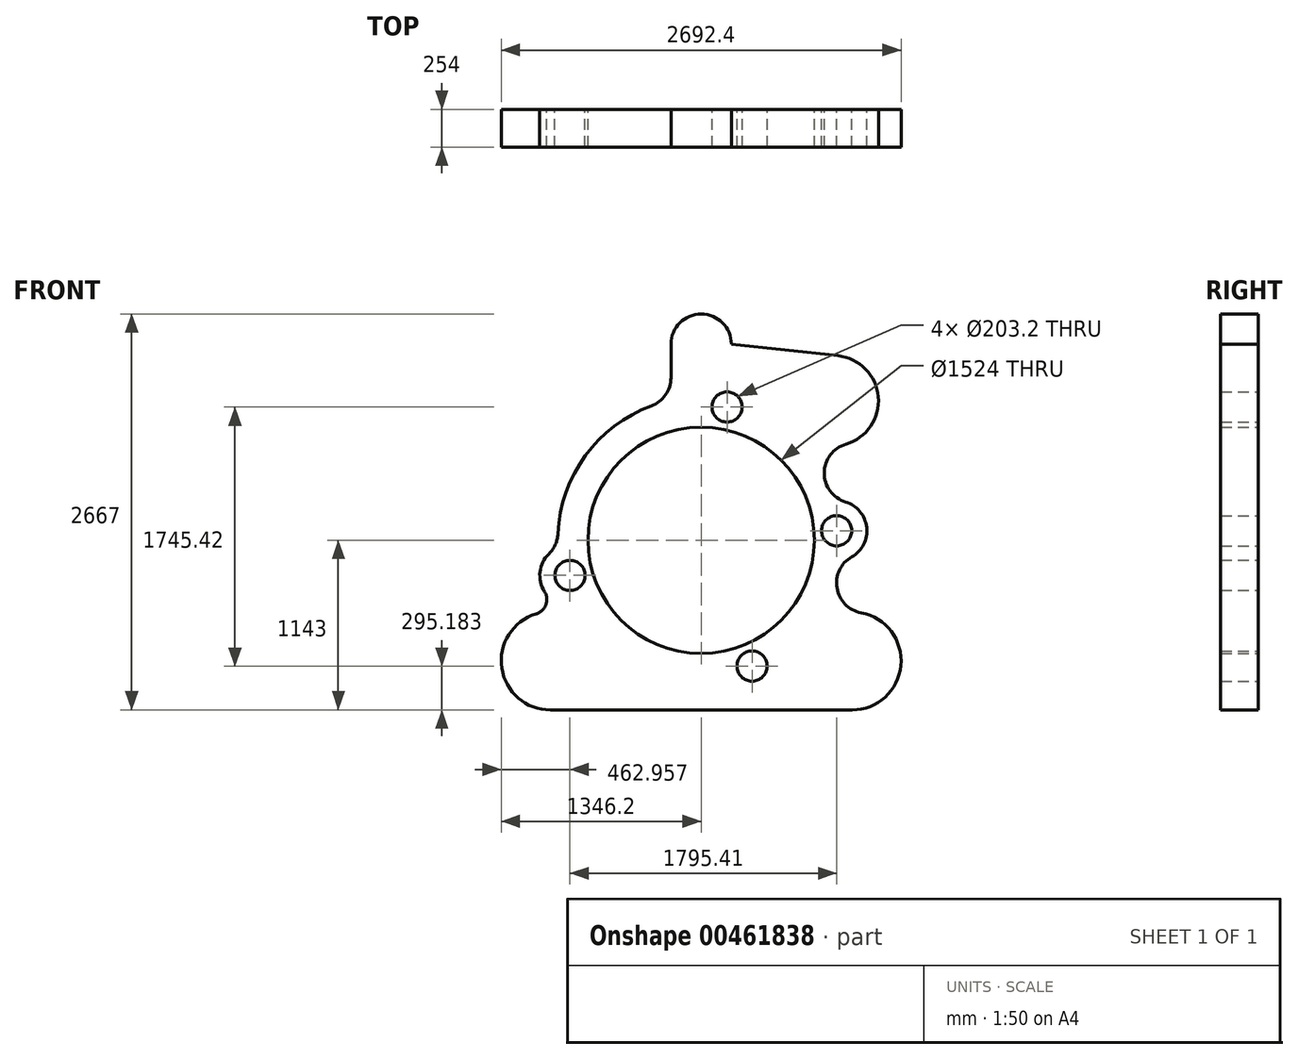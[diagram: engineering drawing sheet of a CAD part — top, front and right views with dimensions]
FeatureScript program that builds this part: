
annotation { "Feature Type Name" : "Feature", "Feature Type Description" : "" }
export const myFeature = defineFeature(function(context is Context, id is Id, definition is map)
    precondition{}
    {
        {
            var Q0;
            Q0=qCreatedBy(makeId("Front.planeOp"),FACE);
            var sketch = newSketch(context, id + "F0", { "sketchPlane" : qUnion([Q0])});
            skCircle(sketch, "E0", {"center": v(0, 0) * mm, "radius": 762 * mm});
            skCircle(sketch, "E1", {"center": v(-883.24, -236.66) * mm, "radius": 101.6 * mm});
            skCircle(sketch, "E2", {"center": v(174.48, 897.6) * mm, "radius": 101.6 * mm});
            skCircle(sketch, "E3", {"center": v(912.17, 63.79) * mm, "radius": 101.6 * mm});
            skCircle(sketch, "E4", {"center": v(342.54, -847.82) * mm, "radius": 101.6 * mm});
            skLineSegment(sketch, "E5", {"start": v(0, -1143) * mm, "end": v(-1016, -1143) * mm});
            skLineSegment(sketch, "E6", {"start": v(-1016, -1143) * mm, "end": v(1016, -1143) * mm});
            skArc(sketch, "E7", {"start": v(-1111.53, -496.72) * mm, "mid": v(-1342.65, -861.08) * mm, "end": v(-1016, -1143) * mm});
            skArc(sketch, "E8", {"start": v(1016, -1143) * mm, "mid": v(1344.77, -843.46) * mm, "end": v(1077.05, -488.3) * mm});
            skArc(sketch, "E9", {"start": v(-1025.2, -91.27) * mm, "mid": v(-1085.05, -212.95) * mm, "end": v(-1055.03, -345.2) * mm});
            skArc(sketch, "E10", {"start": v(-1111.53, -496.72) * mm, "mid": v(-1045.73, -434.96) * mm, "end": v(-1055.03, -345.2) * mm});
            skArc(sketch, "E11", {"start": v(-1025.2, -91.27) * mm, "mid": v(-981.76, -29.07) * mm, "end": v(-964.16, 44.71) * mm});
            skArc(sketch, "E12", {"start": v(203.2, 1320.8) * mm, "mid": v(0, 1524) * mm, "end": v(-203.2, 1320.8) * mm});
            skLineSegment(sketch, "E13", {"start": v(-203.2, 1320.8) * mm, "end": v(-203.2, 1095.44) * mm});
            skArc(sketch, "E14", {"start": v(-335.72, 904.93) * mm, "mid": v(-239.59, 979.4) * mm, "end": v(-203.2, 1095.44) * mm});
            skArc(sketch, "E15.trimOffspring", {"start": v(-335.72, 904.93) * mm, "mid": v(-779.37, 569.38) * mm, "end": v(-964.16, 44.71) * mm});
            skArc(sketch, "E16", {"start": v(1013.4, -112.4) * mm, "mid": v(1114.1, 86.4) * mm, "end": v(971.9, 258) * mm});
            skArc(sketch, "E17", {"start": v(1013.4, -112.4) * mm, "mid": v(914.28, -322.53) * mm, "end": v(1077.05, -488.3) * mm});
            skArc(sketch, "E18", {"start": v(974.58, 647.26) * mm, "mid": v(1192.61, 966.66) * mm, "end": v(921.88, 1242.82) * mm});
            skLineSegment(sketch, "E19", {"start": v(203.2, 1320.8) * mm, "end": v(430.8, 1296.88) * mm});
            skLineSegment(sketch, "E20", {"start": v(203.2, 1320.8) * mm, "end": v(921.88, 1242.82) * mm});
            skArc(sketch, "E21", {"start": v(974.58, 647.26) * mm, "mid": v(828.43, 453.63) * mm, "end": v(971.9, 258) * mm});
            skSolve(sketch);
        }
        {
            var Q0;
            Q0=makeQuery(id+"F0.imprint","IMPRINT",FACE,{"disambiguationData":[TD([[makeQuery(id+"F0.imprint","IMPRINT",EDGE,{"derivedFrom":sQuery(id+"F0.wireOp",EDGE,"E0")}),-1.0]])]});
            extrude(context, id + "F1", {"entities" : qUnion([Q0]), "depth" : 254 * mm});
        }
    });
